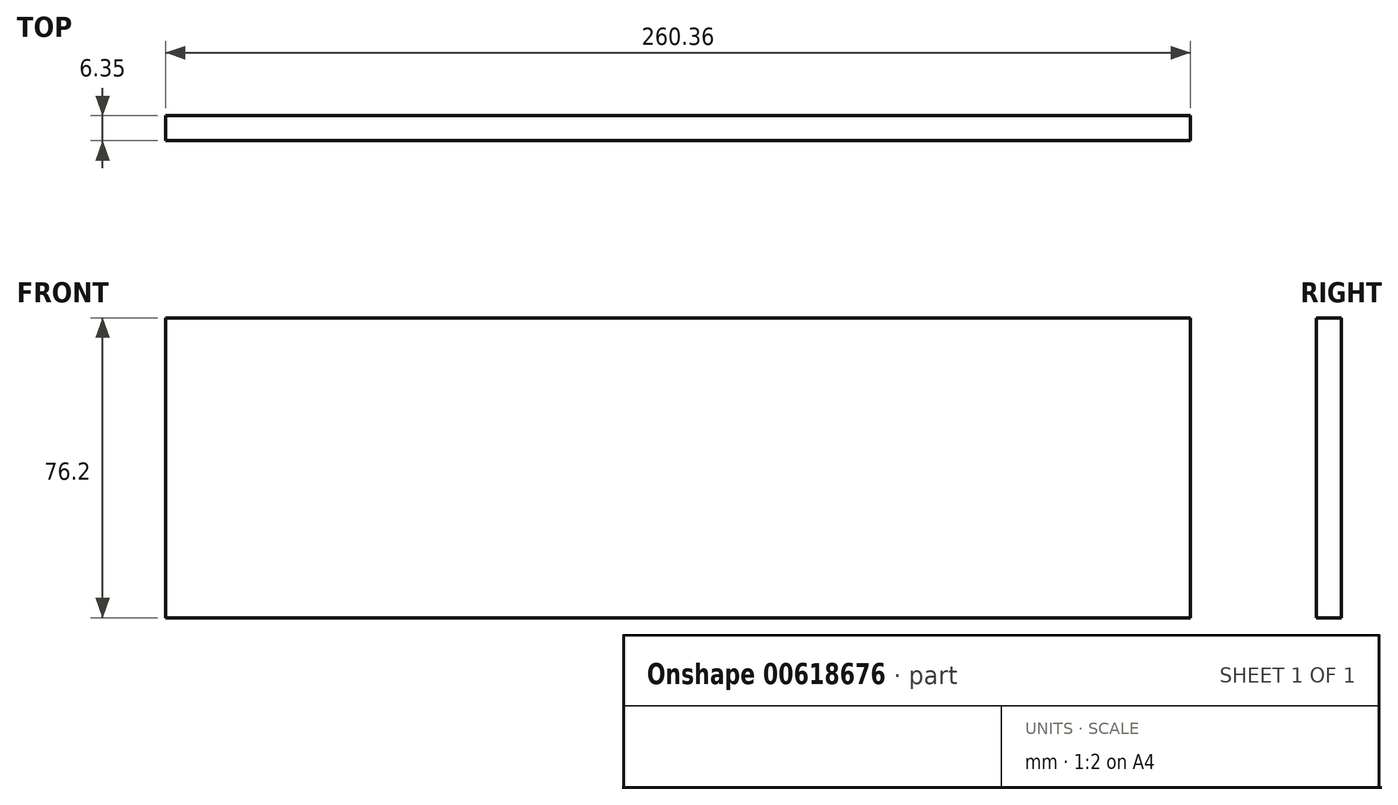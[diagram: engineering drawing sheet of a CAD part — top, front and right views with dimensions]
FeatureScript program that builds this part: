
annotation { "Feature Type Name" : "Feature", "Feature Type Description" : "" }
export const myFeature = defineFeature(function(context is Context, id is Id, definition is map)
    precondition{}
    {
        {
            var Q0;
            Q0=qCreatedBy(makeId("Front.planeOp"),FACE);
            var sketch = newSketch(context, id + "F0", { "sketchPlane" : qUnion([Q0])});
            skLineSegment(sketch, "E0.bottom", {"start": v(130.18, 38.1) * mm, "end": v(-130.18, 38.1) * mm});
            skLineSegment(sketch, "E0.top", {"start": v(130.18, -38.1) * mm, "end": v(-130.18, -38.1) * mm});
            skLineSegment(sketch, "E0.left", {"start": v(130.18, 38.1) * mm, "end": v(130.18, -38.1) * mm});
            skLineSegment(sketch, "E0.right", {"start": v(-130.18, 38.1) * mm, "end": v(-130.18, -38.1) * mm});
            skPoint(sketch, "E0.middle", {"position": v(0, 0) * mm});
            skSolve(sketch);
        }
        {
            var Q0;
            Q0=makeQuery(id+"F0.imprint","IMPRINT",FACE,{"disambiguationData":[TD([[makeQuery(id+"F0.imprint","IMPRINT",EDGE,{"derivedFrom":sQuery(id+"F0.wireOp",EDGE,"E0.bottom")}),1.0]])]});
            extrude(context, id + "F1", {"entities" : qUnion([Q0]), "depth" : 6.35 * mm, "offsetDistance" : 25.4 * mm});
        }
    });
